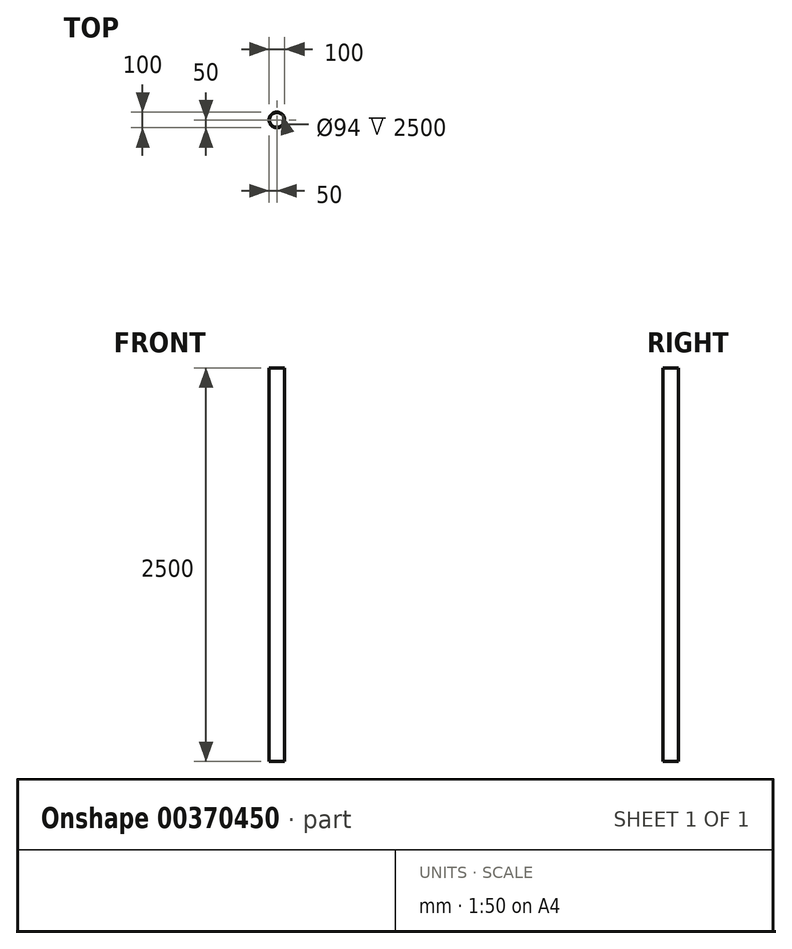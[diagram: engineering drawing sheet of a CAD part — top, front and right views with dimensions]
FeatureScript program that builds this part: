
annotation { "Feature Type Name" : "Feature", "Feature Type Description" : "" }
export const myFeature = defineFeature(function(context is Context, id is Id, definition is map)
    precondition{}
    {
        {
            var Q0;
            Q0=qCreatedBy(makeId("Top.planeOp"),FACE);
            var sketch = newSketch(context, id + "F0", { "sketchPlane" : qUnion([Q0])});
            skCircle(sketch, "E0", {"center": v(0, 0) * mm, "radius": 50 * mm});
            skCircle(sketch, "E1", {"center": v(0, 0) * mm, "radius": 47 * mm});
            skSolve(sketch);
        }
        {
            var Q0;
            Q0=makeQuery(id+"F0.imprint","IMPRINT",FACE,{"disambiguationData":[TD([[makeQuery(id+"F0.imprint","IMPRINT",EDGE,{"derivedFrom":sQuery(id+"F0.wireOp",EDGE,"E0")}),1.0]])]});
            extrude(context, id + "F1", {"entities" : qUnion([Q0]), "depth" : 2500 * mm});
        }
    });
